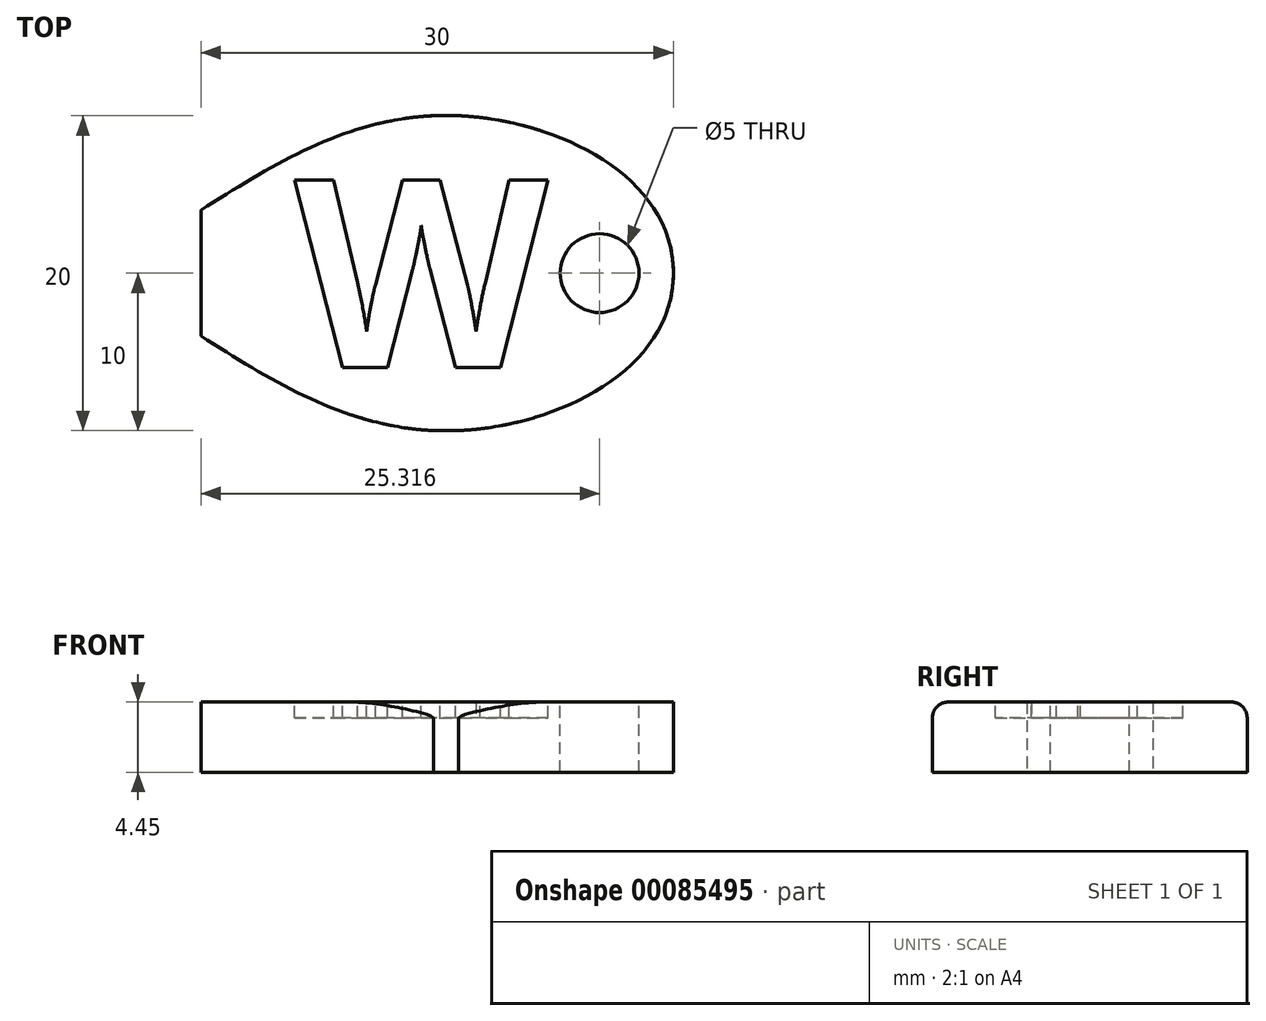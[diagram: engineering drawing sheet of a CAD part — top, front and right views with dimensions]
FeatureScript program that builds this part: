
annotation { "Feature Type Name" : "Feature", "Feature Type Description" : "" }
export const myFeature = defineFeature(function(context is Context, id is Id, definition is map)
    precondition{}
    {
        {
            var Q0;
            Q0=qCreatedBy(makeId("Right.planeOp"),FACE);
            var sketch = newSketch(context, id + "F0", { "sketchPlane" : qUnion([Q0])});
            skCircle(sketch, "E0.cCircle", {"center": v(0, 2.31) * mm, "radius": 2 * mm, "construction": true});
            skLineSegment(sketch, "E0.0", {"start": v(2.34, 3.07) * mm, "end": v(1.45, 0.32) * mm});
            skLineSegment(sketch, "E0.1", {"start": v(1.45, 0.32) * mm, "end": v(-1.45, 0.32) * mm});
            skLineSegment(sketch, "E0.2", {"start": v(-1.45, 0.32) * mm, "end": v(-2.34, 3.07) * mm});
            skLineSegment(sketch, "E0.3", {"start": v(-2.34, 3.07) * mm, "end": v(0, 4.77) * mm});
            skLineSegment(sketch, "E0.4", {"start": v(0, 4.77) * mm, "end": v(2.34, 3.07) * mm});
            skPoint(sketch, "E0.0.midPoint", {"position": v(1.9, 1.7) * mm});
            skSolve(sketch);
        }
        {
            var Q0;
            Q0=makeQuery(id+"F0.imprint","IMPRINT",FACE,{"disambiguationData":[TD([[makeQuery(id+"F0.imprint","IMPRINT",EDGE,{"derivedFrom":sQuery(id+"F0.wireOp",EDGE,"E0.0")}),-1.0]])]});
            extrude(context, id + "F1", {"entities" : qUnion([Q0]), "depth" : 5 * mm});
        }
        {
            var Q0;
            {var subQ0=sQuery(id+"F3.wireOp",EDGE,"E1.bottom");var subQ1=sQuery(id+"F3.wireOp",EDGE,"E1.left");var subQ2=sQuery(id+"F3.wireOp",EDGE,"E1.top");var subQ3=makeQuery(id+"F4.opExtrude","CAP_FACE",FACE,{"disambiguationData":[OSD([subQ0,subQ2,subQ1,sQuery(id+"F3.wireOp",EDGE,"E1.right")])],"isStart":true});Q0=makeQuery(id+"F4.boolean.opBoolean","SPLIT",FACE,{"disambiguationData":[TD([makeQuery(id+"F1.opExtrude","SWEPT_FACE",FACE,{"disambiguationData":[OSD([sQuery(id+"F0.wireOp",EDGE,"E0.2")])]})])],"derivedFrom":subQ3});}
            var Q1;
            Q1=makeQuery(id+"F1.opExtrude","CAP_FACE",FACE,{"disambiguationData":[OSD([sQuery(id+"F0.wireOp",EDGE,"E0.0"),sQuery(id+"F0.wireOp",EDGE,"E0.1"),sQuery(id+"F0.wireOp",EDGE,"E0.2"),sQuery(id+"F0.wireOp",EDGE,"E0.3"),sQuery(id+"F0.wireOp",EDGE,"E0.4")])],"isStart":false});
            cPlane(context, id + "F2", {"entities" : qUnion([Q0, Q1]), "cplaneType" : CPlaneType.OFFSET, "offset" : 10 * mm, "width" : 150 * mm, "height" : 150 * mm});
        }
        {
            var Q0;
            Q0=qCreatedBy(id+"F2.planeOp",FACE);
            var sketch = newSketch(context, id + "F3", { "sketchPlane" : qUnion([Q0])});
            skLineSegment(sketch, "E1.bottom", {"start": v(-4, 4.77) * mm, "end": v(4, 4.77) * mm});
            skLineSegment(sketch, "E1.top", {"start": v(-4, 0.32) * mm, "end": v(4, 0.32) * mm});
            skLineSegment(sketch, "E1.left", {"start": v(-4, 4.77) * mm, "end": v(-4, 0.32) * mm});
            skLineSegment(sketch, "E1.right", {"start": v(4, 4.77) * mm, "end": v(4, 0.32) * mm});
            skPoint(sketch, "E2", {"position": v(0, 0.32) * mm});
            skSolve(sketch);
        }
        {
            var Q0;
            {var subQ0=sQuery(id+"F3.wireOp",EDGE,"E1.left");Q0=makeQuery(id+"F3.imprint","IMPRINT",FACE,{"disambiguationData":[TD([[makeQuery(id+"F3.imprint","IMPRINT",EDGE,{"derivedFrom":subQ0}),1.0]])]});}
            var Q1;
            {var subQ0=makeQuery(id+"F1.opExtrude","CAP_EDGE",EDGE,{"disambiguationData":[OSD([sQuery(id+"F0.wireOp",EDGE,"E0.0")])],"isStart":false});Q1=makeQuery(id+"F3.imprint","IMPRINT",FACE,{"disambiguationData":[TD([[makeQuery(id+"F3.imprint","IMPRINT",EDGE,{"derivedFrom":subQ0}),-1.0]])]});}
            var Q2;
            {var subQ1=sQuery(id+"F3.wireOp",EDGE,"E1.right");Q2=makeQuery(id+"F3.imprint","IMPRINT",FACE,{"disambiguationData":[TD([[makeQuery(id+"F3.imprint","IMPRINT",EDGE,{"derivedFrom":subQ1}),-1.0]])]});}
            extrude(context, id + "F4", {"entities" : qUnion([Q0, Q1, Q2]), "operationType" : NewBodyOperationType.ADD, "depth" : 10 * mm});
        }
        {
            var Q0;
            Q0=makeQuery(id+"F1.opExtrude","CAP_FACE",FACE,{"disambiguationData":[OSD([sQuery(id+"F0.wireOp",EDGE,"E0.0"),sQuery(id+"F0.wireOp",EDGE,"E0.1"),sQuery(id+"F0.wireOp",EDGE,"E0.2"),sQuery(id+"F0.wireOp",EDGE,"E0.3"),sQuery(id+"F0.wireOp",EDGE,"E0.4")])],"isStart":false});
            var Q1;
            Q1=makeQuery(id+"F4.opExtrude","CAP_FACE",FACE,{"disambiguationData":[OSD([sQuery(id+"F3.wireOp",EDGE,"E1.bottom"),sQuery(id+"F3.wireOp",EDGE,"E1.top"),sQuery(id+"F3.wireOp",EDGE,"E1.left"),sQuery(id+"F3.wireOp",EDGE,"E1.right")])],"isStart":true});
            loft(context, id + "F5", {"sheetProfilesArray" : [{ "sheetProfileEntities" : qUnion([Q0]) }, { "sheetProfileEntities" : qUnion([Q1]) }]});
        }
        {
            var Q0;
            Q0=makeQuery(id+"F1.opExtrude","SWEPT_BODY",BODY,{"disambiguationData":[OSD([sQuery(id+"F0.wireOp",EDGE,"E0.0"),sQuery(id+"F0.wireOp",EDGE,"E0.1"),sQuery(id+"F0.wireOp",EDGE,"E0.2"),sQuery(id+"F0.wireOp",EDGE,"E0.3"),sQuery(id+"F0.wireOp",EDGE,"E0.4")])]});
            var Q1;
            Q1=makeQuery(id+"F5.opLoft","SWEPT_BODY",BODY,{"disambiguationData":[OSD([sQuery(id+"F0.wireOp",EDGE,"E0.0"),sQuery(id+"F0.wireOp",EDGE,"E0.1"),sQuery(id+"F0.wireOp",EDGE,"E0.2"),sQuery(id+"F0.wireOp",EDGE,"E0.3"),sQuery(id+"F0.wireOp",EDGE,"E0.4"),sQuery(id+"F3.wireOp",EDGE,"E1.bottom"),sQuery(id+"F3.wireOp",EDGE,"E1.top"),sQuery(id+"F3.wireOp",EDGE,"E1.left"),sQuery(id+"F3.wireOp",EDGE,"E1.right")])]});
            var Q2;
            Q2=makeQuery(id+"F4.opExtrude","SWEPT_BODY",BODY,{"disambiguationData":[OSD([sQuery(id+"F3.wireOp",EDGE,"E1.bottom"),sQuery(id+"F3.wireOp",EDGE,"E1.top"),sQuery(id+"F3.wireOp",EDGE,"E1.left"),sQuery(id+"F3.wireOp",EDGE,"E1.right")])]});
            booleanBodies(context, id + "F6", {"operationType" : BooleanOperationType.UNION, "tools" : qUnion([Q0, Q1, Q2])});
        }
        {
            var Q0;
            Q0=makeQuery(id+"F4.opExtrude","CAP_FACE",FACE,{"disambiguationData":[OSD([sQuery(id+"F3.wireOp",EDGE,"E1.bottom"),sQuery(id+"F3.wireOp",EDGE,"E1.top"),sQuery(id+"F3.wireOp",EDGE,"E1.left"),sQuery(id+"F3.wireOp",EDGE,"E1.right")])],"isStart":false});
            cPlane(context, id + "F7", {"entities" : qUnion([Q0]), "cplaneType" : CPlaneType.OFFSET, "offset" : 10 * mm, "oppositeDirection" : true, "width" : 150 * mm, "height" : 150 * mm});
        }
        {
            var Q0;
            Q0=qCreatedBy(id+"F7.planeOp",FACE);
            var sketch = newSketch(context, id + "F8", { "sketchPlane" : qUnion([Q0])});
            skLineSegment(sketch, "E3.bottom", {"start": v(-4, 4.77) * mm, "end": v(4, 4.77) * mm, "construction": true});
            skLineSegment(sketch, "E3.top", {"start": v(-4, 0.32) * mm, "end": v(4, 0.32) * mm, "construction": true});
            skLineSegment(sketch, "E3.left", {"start": v(-4, 4.77) * mm, "end": v(-4, 0.32) * mm, "construction": true});
            skLineSegment(sketch, "E3.right", {"start": v(4, 4.77) * mm, "end": v(4, 0.32) * mm, "construction": true});
            skLineSegment(sketch, "E4", {"start": v(-4, 2.55) * mm, "end": v(4, 2.55) * mm, "construction": true});
            skPoint(sketch, "E5", {"position": v(4, 4.77) * mm});
            skPoint(sketch, "E6", {"position": v(-4, 0.32) * mm});
            skLineSegment(sketch, "E7", {"start": v(4, 4.77) * mm, "end": v(-4, 0.32) * mm, "construction": true});
            skPoint(sketch, "E8", {"position": v(0, 2.55) * mm});
            skLineSegment(sketch, "E9.bottom", {"start": v(-10, 4.77) * mm, "end": v(10, 4.77) * mm});
            skLineSegment(sketch, "E9.top", {"start": v(-10, 0.32) * mm, "end": v(10, 0.32) * mm});
            skLineSegment(sketch, "E9.left", {"start": v(-10, 4.77) * mm, "end": v(-10, 0.32) * mm});
            skLineSegment(sketch, "E9.right", {"start": v(10, 4.77) * mm, "end": v(10, 0.32) * mm});
            skLineSegment(sketch, "E10", {"start": v(-4, 2.55) * mm, "end": v(-10, 2.55) * mm, "construction": true});
            skLineSegment(sketch, "E11", {"start": v(4, 2.55) * mm, "end": v(10, 2.55) * mm, "construction": true});
            skLineSegment(sketch, "E12", {"start": v(0, 4.77) * mm, "end": v(0, 4.77) * mm});
            skLineSegment(sketch, "E13", {"start": v(0, 0.32) * mm, "end": v(0, 0.32) * mm});
            skSolve(sketch);
        }
        {
            var Q0;
            Q0=makeQuery(id+"F8.imprint","IMPRINT",FACE,{"disambiguationData":[TD([[makeQuery(id+"F8.imprint","IMPRINT",EDGE,{"derivedFrom":sQuery(id+"F8.wireOp",EDGE,"E9.bottom")}),-1.0]])]});
            extrude(context, id + "F9", {"entities" : qUnion([Q0]), "depth" : 30 * mm});
        }
        {
            var Q0;
            Q0=makeQuery(id+"F9.opExtrude","SWEPT_FACE",FACE,{"disambiguationData":[OSD([sQuery(id+"F8.wireOp",EDGE,"E9.bottom")])]});
            var sketch = newSketch(context, id + "F10", { "sketchPlane" : qUnion([Q0])});
            skLineSegment(sketch, "E14", {"start": v(15, 0) * mm, "end": v(49.97, 0) * mm, "construction": true});
            skLineSegment(sketch, "E15", {"start": v(1.27, -4) * mm, "end": v(27.75, -4) * mm, "construction": true});
            skLineSegment(sketch, "E16", {"start": v(15, -4) * mm, "end": v(15, 4) * mm});
            skFitSpline(sketch, "E17", {"points": [v(15, -4) * mm, v(31.35, -10) * mm, v(45, 0) * mm], "startDerivative": vector(30, -19.1) * mm, "endDerivative": vector(0, 37.56) * mm});
            skFitSpline(sketch, "E18.MirrorCS", {"points": [v(15, 4) * mm, v(31.35, 10) * mm, v(45, 0) * mm], "startDerivative": vector(30, 19.1) * mm, "endDerivative": vector(0, -37.56) * mm});
            skSolve(sketch);
        }
        {
            var Q0;
            {var subQ11=sQuery(id+"F10.wireOp",EDGE,"E16");Q0=makeQuery(id+"F10.imprint","IMPRINT",FACE,{"disambiguationData":[TD([[makeQuery(id+"F10.imprint","IMPRINT",EDGE,{"derivedFrom":subQ11}),-1.0]])]});}
            extrude(context, id + "F11", {"entities" : qUnion([Q0]), "operationType" : NewBodyOperationType.INTERSECT, "oppositeDirection" : true, "depth" : 25 * mm});
        }
        {
            var Q0;
            {var subQ9=sQuery(id+"F10.wireOp",EDGE,"E16");Q0=makeQuery(id+"F10.imprint","IMPRINT",FACE,{"disambiguationData":[TD([[makeQuery(id+"F10.imprint","IMPRINT",EDGE,{"derivedFrom":subQ9}),-1.0]])]});}
            var sketch = newSketch(context, id + "F12", { "sketchPlane" : qUnion([Q0])});
            skText(sketch, "E19", { "text": "W", "fontName": "OpenSans-Bold.ttf"});
            skPoint(sketch, "E20", {"position": v(29, 0) * mm});
            const initialGuessF12  = {"E19": [0.02094, -0.006, 1, 0, 0.012]};
            skSetInitialGuess(sketch, initialGuessF12);
            skSolve(sketch);
        }
        {
            var Q0;
            Q0 = qSketchRegion(id + "F12", true);
            extrude(context, id + "F13", {"entities" : qUnion([Q0]), "operationType" : NewBodyOperationType.REMOVE, "oppositeDirection" : true, "depth" : 1 * mm});
        }
        {
            var Q0;
            Q0=makeQuery(id+"F1.opExtrude","SWEPT_BODY",BODY,{"disambiguationData":[OSD([sQuery(id+"F0.wireOp",EDGE,"E0.0"),sQuery(id+"F0.wireOp",EDGE,"E0.1"),sQuery(id+"F0.wireOp",EDGE,"E0.2"),sQuery(id+"F0.wireOp",EDGE,"E0.3"),sQuery(id+"F0.wireOp",EDGE,"E0.4")])]});
            var Q1;
            Q1=makeQuery(id+"F9.opExtrude","SWEPT_BODY",BODY,{"disambiguationData":[OSD([sQuery(id+"F8.wireOp",EDGE,"E9.bottom"),sQuery(id+"F8.wireOp",EDGE,"E9.top"),sQuery(id+"F8.wireOp",EDGE,"E9.left"),sQuery(id+"F8.wireOp",EDGE,"E9.right")])]});
            booleanBodies(context, id + "F14", {"operationType" : BooleanOperationType.UNION, "tools" : qUnion([Q0, Q1])});
        }
        {
            var Q0;
            {var subQ2=sQuery(id+"F3.wireOp",EDGE,"E1.left");var subQ4=sQuery(id+"F3.wireOp",EDGE,"E1.bottom");var subQ5=makeQuery(id+"F4.opExtrude","SWEPT_FACE",FACE,{"disambiguationData":[OSD([subQ4])]});Q0=makeQuery(id+"F14.opBoolean","MERGE",FACE,{"derivedFrom":[makeQuery(id+"F9.opExtrude","SWEPT_FACE",FACE,{"disambiguationData":[OSD([sQuery(id+"F8.wireOp",EDGE,"E9.bottom")])]}),makeQuery(id+"F13.boolean.opBoolean","SPLIT",FACE,{"disambiguationData":[TD([makeQuery(id+"F4.opExtrude","SWEPT_FACE",FACE,{"disambiguationData":[OSD([subQ2])]})])],"derivedFrom":subQ5}),makeQuery(id+"F13.boolean.opBoolean","SPLIT",FACE,{"disambiguationData":[TD([makeQuery(id+"F13.opExtrude","SWEPT_FACE",FACE,{"disambiguationData":[OSD([sQuery(id+"F12.wireOp",EDGE,"E19.sketch_text.stroke-10")])]})])],"derivedFrom":subQ5})]});}
            var sketch = newSketch(context, id + "F15", { "sketchPlane" : qUnion([Q0])});
            skCircle(sketch, "E21", {"center": v(40.32, 0) * mm, "radius": 2.5 * mm});
            skLineSegment(sketch, "E22", {"start": v(15, 0) * mm, "end": v(50.7, 0) * mm, "construction": true});
            skSolve(sketch);
        }
        {
            var Q0;
            Q0=makeQuery(id+"F15.imprint","IMPRINT",FACE,{"disambiguationData":[TD([[makeQuery(id+"F15.imprint","IMPRINT",EDGE,{"derivedFrom":sQuery(id+"F15.wireOp",EDGE,"E21")}),1.0]])]});
            var Q1;
            {var subQ0=sQuery(id+"F3.wireOp",EDGE,"E1.top");var subQ1=sQuery(id+"F0.wireOp",EDGE,"E0.1");Q1=makeQuery(id+"F14.opBoolean","MERGE",FACE,{"derivedFrom":[makeQuery(id+"F6.opBoolean","MERGE",FACE,{"derivedFrom":[makeQuery(id+"F1.opExtrude","SWEPT_FACE",FACE,{"disambiguationData":[OSD([subQ1])]}),makeQuery(id+"F4.opExtrude","SWEPT_FACE",FACE,{"disambiguationData":[OSD([subQ0])]}),makeQuery(id+"F5.opLoft","SWEPT_FACE",FACE,{"disambiguationData":[OSD([sQuery(id+"F0.wireOp",EDGE,"E0.0"),subQ1,sQuery(id+"F0.wireOp",EDGE,"E0.2"),subQ0,sQuery(id+"F3.wireOp",EDGE,"E1.left"),sQuery(id+"F3.wireOp",EDGE,"E1.right")])]})]}),makeQuery(id+"F9.opExtrude","SWEPT_FACE",FACE,{"disambiguationData":[OSD([sQuery(id+"F8.wireOp",EDGE,"E9.top")])]})]});}
            extrude(context, id + "F16", {"entities" : qUnion([Q0]), "operationType" : NewBodyOperationType.REMOVE, "endBound" : BoundingType.UP_TO_SURFACE, "oppositeDirection" : true, "endBoundEntityFace" : qUnion([Q1]), "depth" : 25 * mm});
        }
        {
            var Q0;
            Q0=makeQuery(id+"F16.boolean.opBoolean","COPY",EDGE,{"derivedFrom":makeQuery(id+"F16.opExtrude","CAP_EDGE",EDGE,{"disambiguationData":[OSD([sQuery(id+"F15.wireOp",EDGE,"E21")])],"isStart":true})});
            var Q1;
            {var subQ0=sQuery(id+"F10.wireOp",EDGE,"E18.MirrorCS");var subQ1=sQuery(id+"F8.wireOp",EDGE,"E9.bottom");Q1=makeQuery(id+"F11.boolean.opBoolean","COPY",EDGE,{"derivedFrom":makeQuery(id+"F11.boolean.toolComplement.opBoolean","COPY",EDGE,{"derivedFrom":makeQuery(id+"F11.opExtrude","CAP_EDGE",EDGE,{"disambiguationData":[OSD([subQ0]),TDD([makeQuery(id+"F10.imprint","IMPRINT",EDGE,{"disambiguationData":[TD([[makeQuery(id+"F10.imprint","INTERSECT",VERTEX,{"derivedFrom":[makeQuery(id+"F9.opExtrude","CAP_EDGE",EDGE,{"disambiguationData":[OSD([subQ1])],"isStart":false}),sQuery(id+"F10.wireOp",EDGE,"E17"),subQ0]}),1.0]])],"derivedFrom":subQ0})])],"isStart":true})})});}
            var Q2;
            {var subQ0=sQuery(id+"F10.wireOp",EDGE,"E18.MirrorCS");var subQ1=sQuery(id+"F8.wireOp",EDGE,"E9.bottom");Q2=makeQuery(id+"F11.boolean.opBoolean","COPY",EDGE,{"derivedFrom":makeQuery(id+"F11.boolean.toolComplement.opBoolean","COPY",EDGE,{"derivedFrom":makeQuery(id+"F11.opExtrude","CAP_EDGE",EDGE,{"disambiguationData":[OSD([subQ0]),TDD([makeQuery(id+"F10.imprint","IMPRINT",EDGE,{"disambiguationData":[TD([[makeQuery(id+"F10.imprint","INTERSECT",VERTEX,{"derivedFrom":[makeQuery(id+"F9.opExtrude","CAP_EDGE",EDGE,{"disambiguationData":[OSD([subQ1])],"isStart":true}),sQuery(id+"F10.wireOp",EDGE,"E16"),subQ0]}),-1.0]])],"derivedFrom":subQ0})])],"isStart":true})})});}
            var Q3;
            Q3=makeQuery(id+"F9.opExtrude","SWEPT_EDGE",EDGE,{"disambiguationData":[OSD([sQuery(id+"F8.wireOp",EDGE,"E9.bottom"),sQuery(id+"F8.wireOp",EDGE,"E9.right")])]});
            var Q4;
            {var subQ0=sQuery(id+"F10.wireOp",EDGE,"E17");var subQ1=sQuery(id+"F8.wireOp",EDGE,"E9.bottom");Q4=makeQuery(id+"F11.boolean.opBoolean","COPY",EDGE,{"derivedFrom":makeQuery(id+"F11.boolean.toolComplement.opBoolean","COPY",EDGE,{"derivedFrom":makeQuery(id+"F11.opExtrude","CAP_EDGE",EDGE,{"disambiguationData":[OSD([subQ0]),TDD([makeQuery(id+"F10.imprint","IMPRINT",EDGE,{"disambiguationData":[TD([[makeQuery(id+"F10.imprint","INTERSECT",VERTEX,{"derivedFrom":[makeQuery(id+"F9.opExtrude","CAP_EDGE",EDGE,{"disambiguationData":[OSD([subQ1])],"isStart":true}),sQuery(id+"F10.wireOp",EDGE,"E16"),subQ0]}),-1.0]])],"derivedFrom":subQ0})])],"isStart":true})})});}
            var Q5;
            Q5=makeQuery(id+"F9.opExtrude","SWEPT_EDGE",EDGE,{"disambiguationData":[OSD([sQuery(id+"F8.wireOp",EDGE,"E9.bottom"),sQuery(id+"F8.wireOp",EDGE,"E9.left")])]});
            var Q6;
            {var subQ0=sQuery(id+"F10.wireOp",EDGE,"E17");var subQ1=sQuery(id+"F8.wireOp",EDGE,"E9.bottom");Q6=makeQuery(id+"F11.boolean.opBoolean","COPY",EDGE,{"derivedFrom":makeQuery(id+"F11.boolean.toolComplement.opBoolean","COPY",EDGE,{"derivedFrom":makeQuery(id+"F11.opExtrude","CAP_EDGE",EDGE,{"disambiguationData":[OSD([subQ0]),TDD([makeQuery(id+"F10.imprint","IMPRINT",EDGE,{"disambiguationData":[TD([[makeQuery(id+"F10.imprint","INTERSECT",VERTEX,{"derivedFrom":[makeQuery(id+"F9.opExtrude","CAP_EDGE",EDGE,{"disambiguationData":[OSD([subQ1])],"isStart":false}),subQ0,sQuery(id+"F10.wireOp",EDGE,"E18.MirrorCS")]}),1.0]])],"derivedFrom":subQ0})])],"isStart":true})})});}
            fillet(context, id + "F17", {"entities" : qUnion([Q0, Q1, Q2, Q3, Q4, Q5, Q6]), "radius" : 1 * mm, "tangentPropagation" : true, "allowEdgeOverflow" : false});
        }
    });
